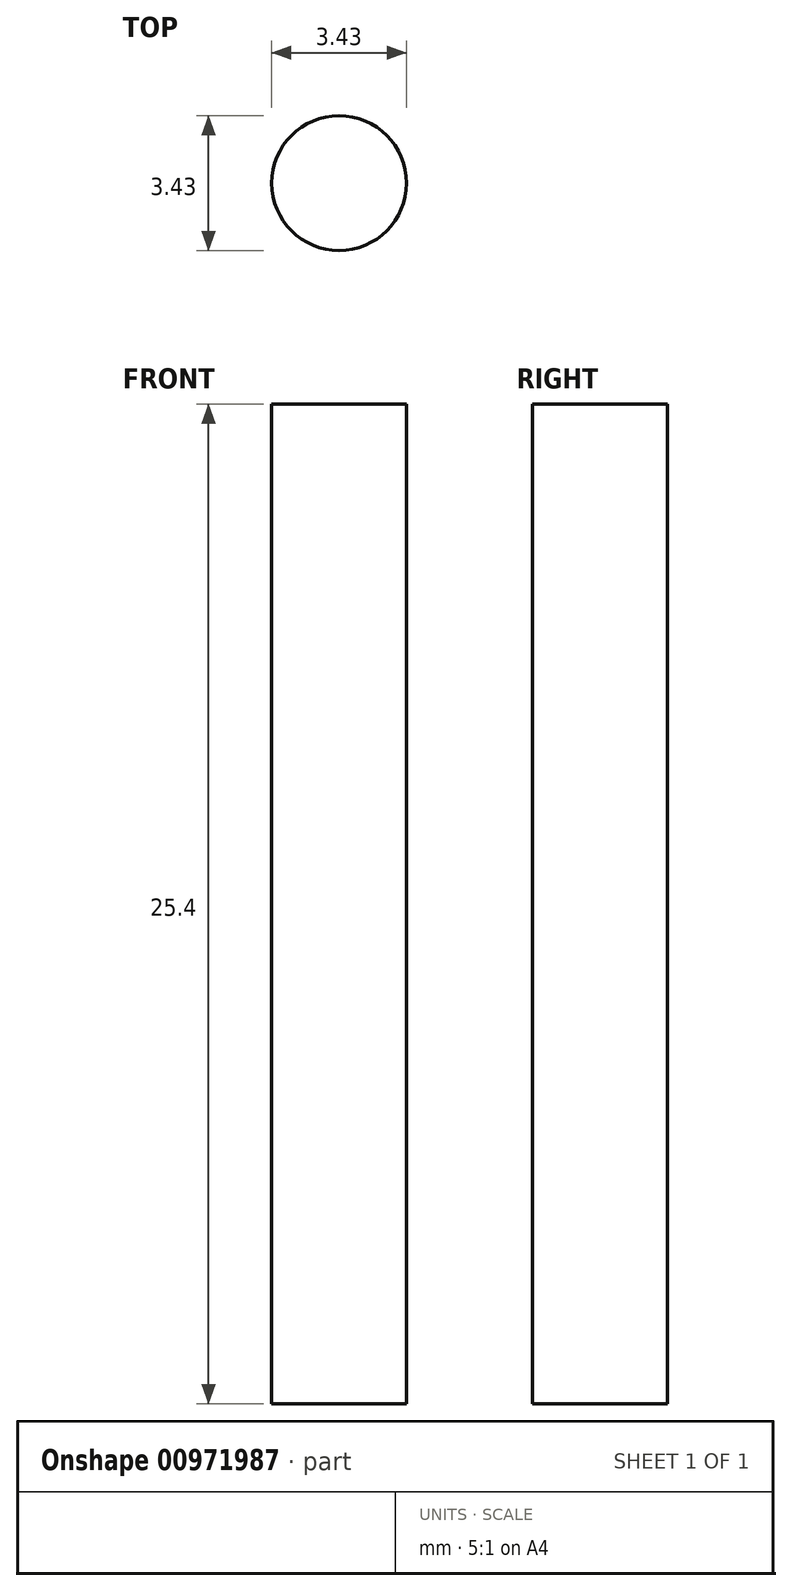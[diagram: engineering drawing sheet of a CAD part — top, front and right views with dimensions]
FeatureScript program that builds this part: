
annotation { "Feature Type Name" : "Feature", "Feature Type Description" : "" }
export const myFeature = defineFeature(function(context is Context, id is Id, definition is map)
    precondition{}
    {
        {
            var Q0;
            Q0=qCreatedBy(makeId("Top.planeOp"),FACE);
            var sketch = newSketch(context, id + "F0", { "sketchPlane" : qUnion([Q0])});
            skCircle(sketch, "E0", {"center": v(-61.85, -18.23) * mm, "radius": 1.71 * mm});
            skSolve(sketch);
        }
        {
            var Q0;
            Q0=makeQuery(id+"F0.imprint","IMPRINT",FACE,{"disambiguationData":[TD([[makeQuery(id+"F0.imprint","IMPRINT",EDGE,{"derivedFrom":sQuery(id+"F0.wireOp",EDGE,"E0")}),1.0]])]});
            extrude(context, id + "F1", {"entities" : qUnion([Q0]), "depth" : 25.4 * mm, "offsetDistance" : 25.4 * mm});
        }
    });
